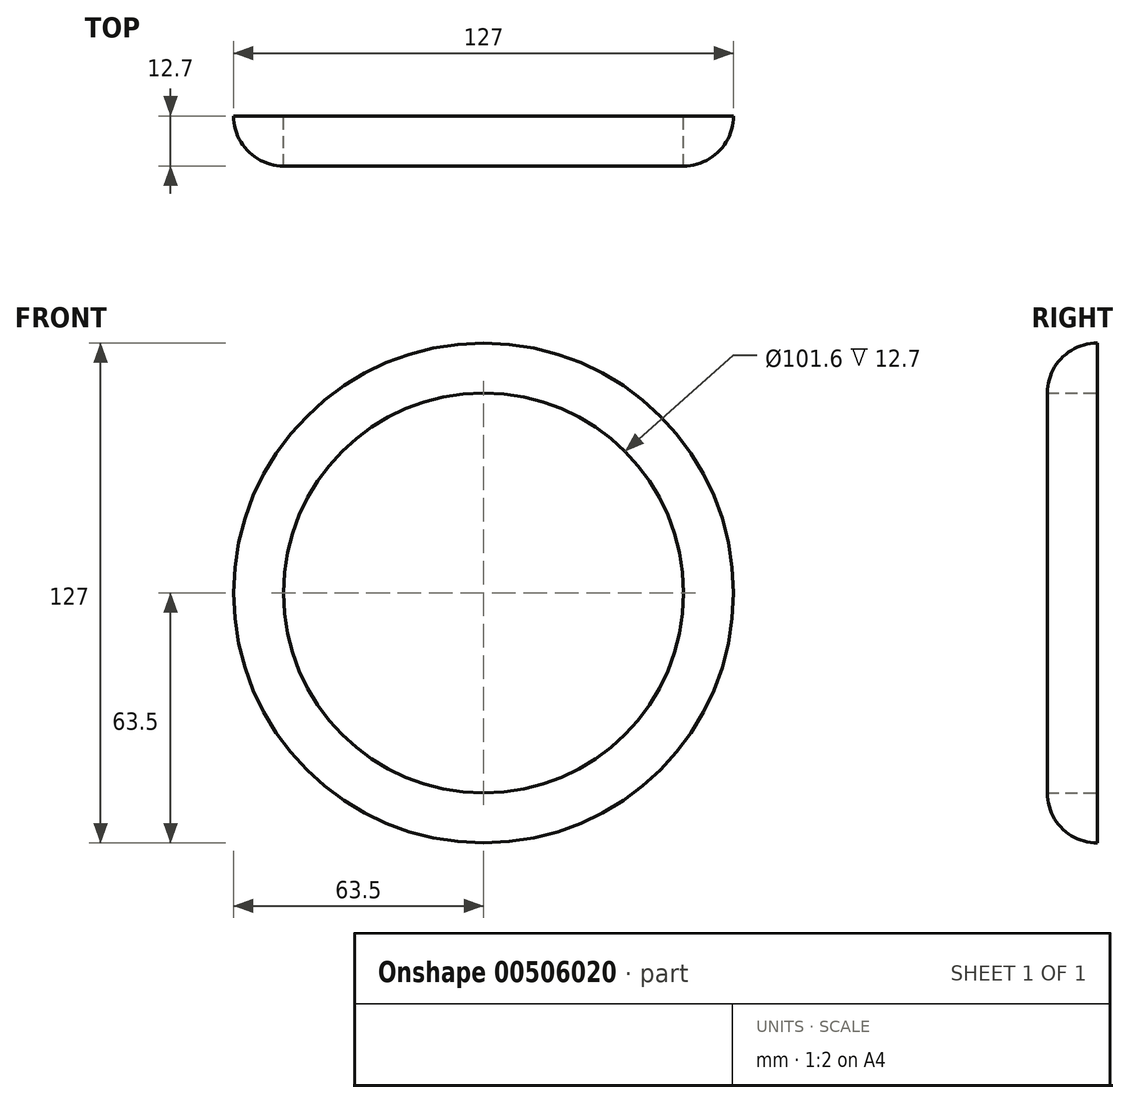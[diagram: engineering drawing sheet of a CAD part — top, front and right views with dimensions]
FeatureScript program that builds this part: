
annotation { "Feature Type Name" : "Feature", "Feature Type Description" : "" }
export const myFeature = defineFeature(function(context is Context, id is Id, definition is map)
    precondition{}
    {
        {
            var Q0;
            Q0=qCreatedBy(makeId("Front.planeOp"),FACE);
            var sketch = newSketch(context, id + "F0", { "sketchPlane" : qUnion([Q0])});
            skCircle(sketch, "E0", {"center": v(0, 0) * mm, "radius": 63.5 * mm});
            skCircle(sketch, "E1", {"center": v(0, 0) * mm, "radius": 50.8 * mm});
            skSolve(sketch);
        }
        {
            var Q0;
            Q0 = qSketchRegion(id + "F0", true);
            extrude(context, id + "F1", {"entities" : qUnion([Q0]), "offsetDistance" : 25.4 * mm, "depth" : 12.7 * mm});
        }
        {
            var Q0;
            Q0=makeQuery(id+"F1.opExtrude","CAP_EDGE",EDGE,{"disambiguationData":[OSD([sQuery(id+"F0.wireOp",EDGE,"E0")])],"isStart":false});
            fillet(context, id + "F2", {"entities" : qUnion([Q0]), "tangentPropagation" : true, "radius" : 12.7 * mm, "defaultsChanged" : true, "vertexSettings" : [], "allowEdgeOverflow" : false});
        }
    });
